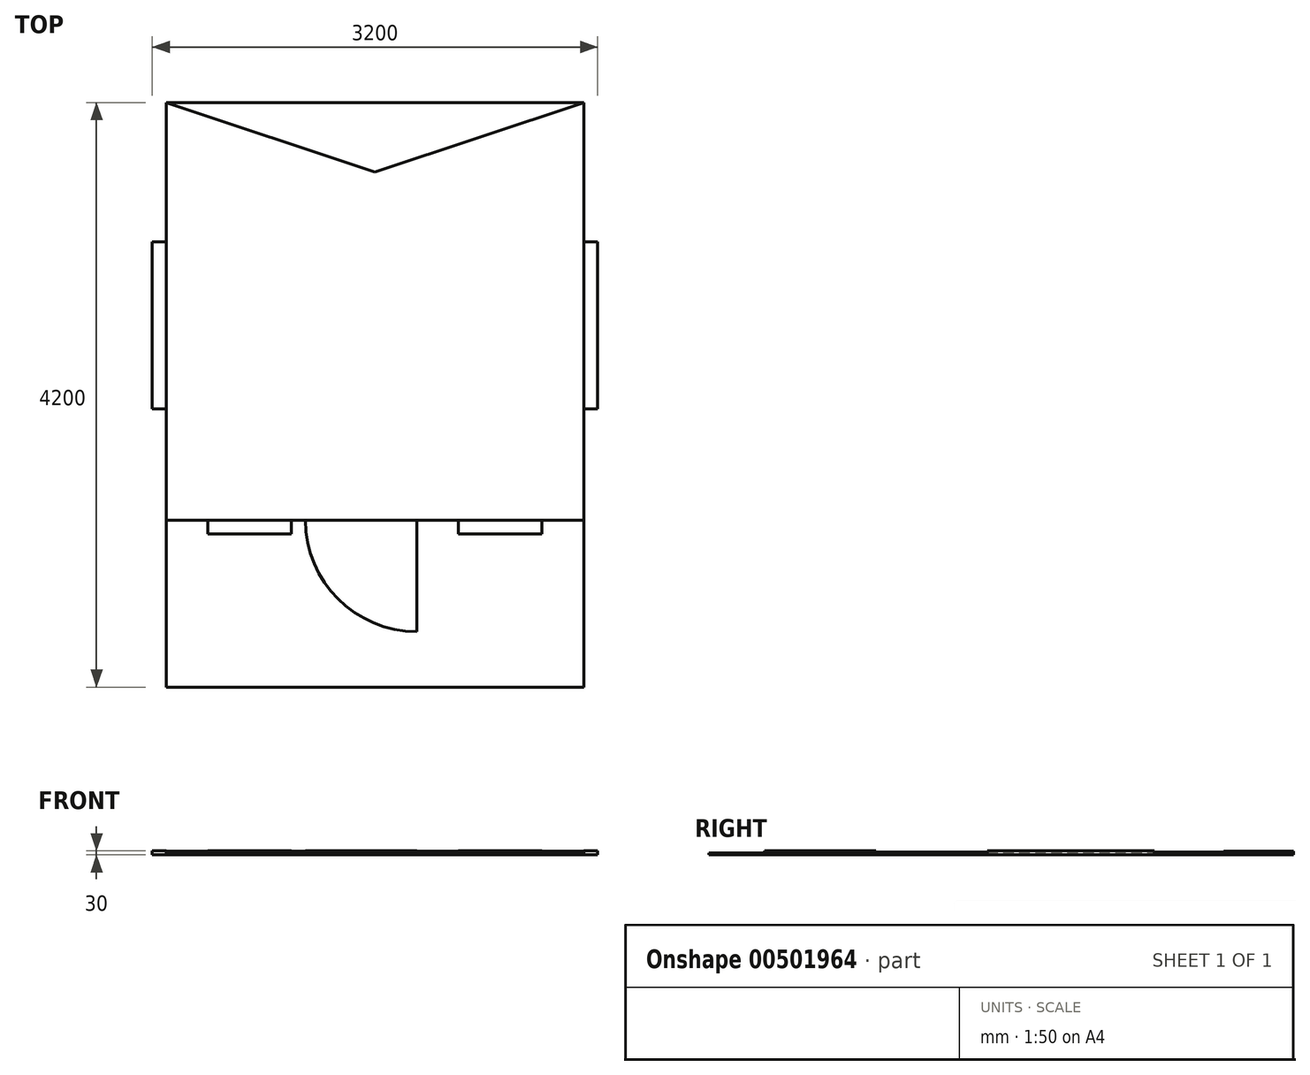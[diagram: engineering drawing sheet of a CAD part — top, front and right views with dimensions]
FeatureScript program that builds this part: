
annotation { "Feature Type Name" : "Feature", "Feature Type Description" : "" }
export const myFeature = defineFeature(function(context is Context, id is Id, definition is map)
    precondition{}
    {
        {
            var Q0;
            Q0=qCreatedBy(makeId("Top.planeOp"),FACE);
            var sketch = newSketch(context, id + "F0", { "sketchPlane" : qUnion([Q0])});
            skLineSegment(sketch, "E0", {"start": v(0, 0) * mm, "end": v(0, 4200) * mm});
            skLineSegment(sketch, "E1", {"start": v(0, 4200) * mm, "end": v(3000, 4200) * mm});
            skLineSegment(sketch, "E2", {"start": v(3000, 4200) * mm, "end": v(3000, 0) * mm});
            skLineSegment(sketch, "E3", {"start": v(3000, 0) * mm, "end": v(0, 0) * mm});
            skLineSegment(sketch, "E4", {"start": v(0, 1200) * mm, "end": v(3000, 1200) * mm});
            skLineSegment(sketch, "E5", {"start": v(1800, 1200) * mm, "end": v(1800, 400) * mm});
            skArc(sketch, "E6", {"start": v(1000, 1200) * mm, "mid": v(1234.31, 634.31) * mm, "end": v(1800, 400) * mm});
            skLineSegment(sketch, "E7", {"start": v(300, 1200) * mm, "end": v(300, 1100) * mm});
            skLineSegment(sketch, "E8", {"start": v(300, 1100) * mm, "end": v(900, 1100) * mm});
            skLineSegment(sketch, "E9", {"start": v(900, 1100) * mm, "end": v(900, 1200) * mm});
            skLineSegment(sketch, "E10", {"start": v(2700, 1200) * mm, "end": v(2700, 1100) * mm});
            skLineSegment(sketch, "E11", {"start": v(2700, 1100) * mm, "end": v(2100, 1100) * mm});
            skLineSegment(sketch, "E12", {"start": v(2100, 1100) * mm, "end": v(2100, 1200) * mm});
            skLineSegment(sketch, "E13", {"start": v(3000, 2000) * mm, "end": v(3100, 2000) * mm});
            skLineSegment(sketch, "E14", {"start": v(3100, 2000) * mm, "end": v(3100, 3200) * mm});
            skLineSegment(sketch, "E15", {"start": v(3100, 3200) * mm, "end": v(3000, 3200) * mm});
            skLineSegment(sketch, "E16", {"start": v(0, 3200) * mm, "end": v(-100, 3200) * mm});
            skLineSegment(sketch, "E17", {"start": v(-100, 3200) * mm, "end": v(-100, 2000) * mm});
            skLineSegment(sketch, "E18", {"start": v(-100, 2000) * mm, "end": v(0, 2000) * mm});
            skLineSegment(sketch, "E19", {"start": v(0, 4200) * mm, "end": v(1500, 3700) * mm});
            skLineSegment(sketch, "E20", {"start": v(1500, 3700) * mm, "end": v(3000, 4200) * mm});
            skSolve(sketch);
        }
        {
            var Q0;
            {var subQ0=sQuery(id+"F0.wireOp",EDGE,"l9Eud7ub-VShh-K3UX-XgTZ-0GMJ4HxS2q9c");Q0=makeQuery(id+"F0.imprint","IMPRINT",FACE,{"disambiguationData":[TD([[makeQuery(id+"F0.imprint","IMPRINT",EDGE,{"derivedFrom":subQ0}),-1.0]])]});}
            var Q1;
            {var subQ2=sQuery(id+"F0.wireOp",EDGE,"JvAI2fed-3nD5-ySdd-6CHk-Oy05x6ShATgp");Q1=makeQuery(id+"F0.imprint","IMPRINT",FACE,{"disambiguationData":[TD([[makeQuery(id+"F0.imprint","IMPRINT",EDGE,{"derivedFrom":subQ2}),1.0]])]});}
            var Q2;
            {var subQ1=sQuery(id+"F0.wireOp",EDGE,"vRRi0WPc-OtRp-V3Je-d8cZ-cZsQz7gKr7FB");Q2=makeQuery(id+"F0.imprint","IMPRINT",FACE,{"disambiguationData":[TD([[makeQuery(id+"F0.imprint","IMPRINT",EDGE,{"derivedFrom":subQ1}),1.0]])]});}
            var Q3;
            {var subQ0=sQuery(id+"F0.wireOp",EDGE,"QlfCJvkj-hnin-aMbN-BNJu-tL6u5rHZoNYO");Q3=makeQuery(id+"F0.imprint","IMPRINT",FACE,{"disambiguationData":[TD([[makeQuery(id+"F0.imprint","IMPRINT",EDGE,{"derivedFrom":subQ0}),1.0]])]});}
            var Q4;
            {var subQ0=sQuery(id+"F0.wireOp",EDGE,"YJlJ8WF4-1fWf-lRlY-H7on-bmglhUY8gcYo");Q4=makeQuery(id+"F0.imprint","IMPRINT",FACE,{"disambiguationData":[TD([[makeQuery(id+"F0.imprint","IMPRINT",EDGE,{"derivedFrom":subQ0}),1.0]])]});}
            var Q5;
            {var subQ9=sQuery(id+"F0.wireOp",EDGE,"E1");Q5=makeQuery(id+"F0.imprint","IMPRINT",FACE,{"disambiguationData":[TD([[makeQuery(id+"F0.imprint","IMPRINT",EDGE,{"derivedFrom":subQ9}),-1.0]])]});}
            extrude(context, id + "F1", {"entities" : qUnion([Q0, Q1, Q2, Q3, Q4, Q5]), "depth" : 25 * mm});
        }
        {
            var Q0;
            {var subQ5=sQuery(id+"F0.wireOp",EDGE,"NRW4N26K-VaIV-sUls-tDlY-8iYoBh4ajsQ5");Q0=makeQuery(id+"F0.imprint","IMPRINT",FACE,{"disambiguationData":[TD([[makeQuery(id+"F0.imprint","IMPRINT",EDGE,{"derivedFrom":subQ5}),1.0]])]});}
            var Q1;
            {var subQ0=sQuery(id+"F0.wireOp",EDGE,"E16");Q1=makeQuery(id+"F0.imprint","IMPRINT",FACE,{"disambiguationData":[TD([[makeQuery(id+"F0.imprint","IMPRINT",EDGE,{"derivedFrom":subQ0}),1.0]])]});}
            var Q2;
            {var subQ0=sQuery(id+"F0.wireOp",EDGE,"E13");Q2=makeQuery(id+"F0.imprint","IMPRINT",FACE,{"disambiguationData":[TD([[makeQuery(id+"F0.imprint","IMPRINT",EDGE,{"derivedFrom":subQ0}),1.0]])]});}
            var Q3;
            {var subQ0=sQuery(id+"F0.wireOp",EDGE,"E10");Q3=makeQuery(id+"F0.imprint","IMPRINT",FACE,{"disambiguationData":[TD([[makeQuery(id+"F0.imprint","IMPRINT",EDGE,{"derivedFrom":subQ0}),-1.0]])]});}
            var Q4;
            {var subQ0=sQuery(id+"F0.wireOp",EDGE,"E7");Q4=makeQuery(id+"F0.imprint","IMPRINT",FACE,{"disambiguationData":[TD([[makeQuery(id+"F0.imprint","IMPRINT",EDGE,{"derivedFrom":subQ0}),1.0]])]});}
            extrude(context, id + "F2", {"entities" : qUnion([Q0, Q1, Q2, Q3, Q4]), "operationType" : NewBodyOperationType.ADD, "depth" : 30 * mm});
        }
        {
            var Q0;
            {var subQ7=sQuery(id+"F0.wireOp",EDGE,"vRRi0WPc-OtRp-V3Je-d8cZ-cZsQz7gKr7FB");Q0=makeQuery(id+"F0.imprint","IMPRINT",FACE,{"disambiguationData":[TD([[makeQuery(id+"F0.imprint","IMPRINT",EDGE,{"derivedFrom":subQ7}),-1.0]])]});}
            var Q1;
            {var subQ0=sQuery(id+"F0.wireOp",EDGE,"E5");Q1=makeQuery(id+"F0.imprint","IMPRINT",FACE,{"disambiguationData":[TD([[makeQuery(id+"F0.imprint","IMPRINT",EDGE,{"derivedFrom":subQ0}),-1.0]])]});}
            extrude(context, id + "F3", {"entities" : qUnion([Q0, Q1]), "operationType" : NewBodyOperationType.ADD, "depth" : 30 * mm});
        }
        {
            var Q0;
            {var subQ8=sQuery(id+"F0.wireOp",EDGE,"E3");Q0=makeQuery(id+"F0.imprint","IMPRINT",FACE,{"disambiguationData":[TD([[makeQuery(id+"F0.imprint","IMPRINT",EDGE,{"derivedFrom":subQ8}),-1.0]])]});}
            extrude(context, id + "F4", {"entities" : qUnion([Q0]), "operationType" : NewBodyOperationType.ADD, "depth" : 15 * mm});
        }
        {
            var Q0;
            {var subQ13=sQuery(id+"F0.wireOp",EDGE,"E19");Q0=makeQuery(id+"F0.imprint","IMPRINT",FACE,{"disambiguationData":[TD([[makeQuery(id+"F0.imprint","IMPRINT",EDGE,{"derivedFrom":subQ13}),-1.0]])]});}
            extrude(context, id + "F5", {"entities" : qUnion([Q0]), "operationType" : NewBodyOperationType.ADD, "depth" : 20 * mm});
        }
    });
